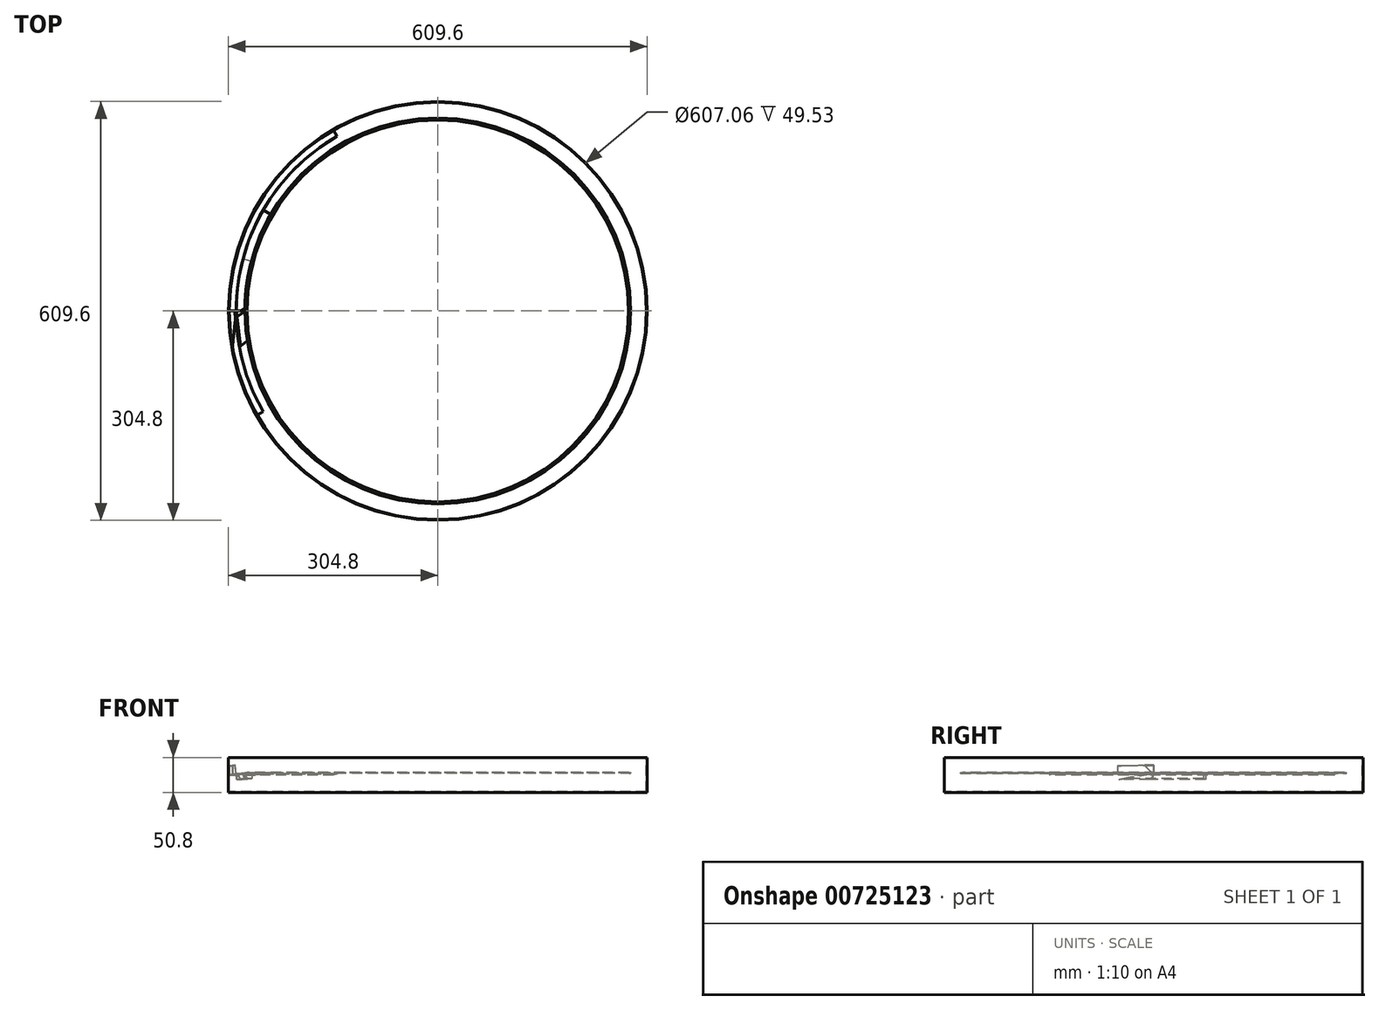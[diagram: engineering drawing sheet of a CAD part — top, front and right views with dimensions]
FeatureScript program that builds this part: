
annotation { "Feature Type Name" : "Feature", "Feature Type Description" : "" }
export const myFeature = defineFeature(function(context is Context, id is Id, definition is map)
    precondition{}
    {
        {
            var Q0;
            Q0=qCreatedBy(makeId("Front.planeOp"),FACE);
            var sketch = newSketch(context, id + "F0", { "sketchPlane" : qUnion([Q0])});
            skLineSegment(sketch, "E0.left", {"start": v(-304.8, -3.12) * mm, "end": v(-304.8, -28.52) * mm});
            skPoint(sketch, "E1.orphan", {"position": v(-304.8, 0) * mm});
            skLineSegment(sketch, "E2", {"start": v(-304.8, -3.12) * mm, "end": v(-304.8, 22.28) * mm});
            skLineSegment(sketch, "E3", {"start": v(-304.8, 22.28) * mm, "end": v(-303.53, 22.28) * mm});
            skLineSegment(sketch, "E4", {"start": v(-303.53, 22.28) * mm, "end": v(-303.53, -2.74) * mm});
            skLineSegment(sketch, "E5", {"start": v(-304.8, -28.52) * mm, "end": v(0, -28.52) * mm});
            skLineSegment(sketch, "E6", {"start": v(-303.53, -27.25) * mm, "end": v(-303.53, -4.1) * mm});
            skLineSegment(sketch, "E7", {"start": v(-303.53, -27.25) * mm, "end": v(0, -27.25) * mm});
            skLineSegment(sketch, "E8", {"start": v(0, -28.52) * mm, "end": v(0, -27.25) * mm});
            skLineSegment(sketch, "E9", {"start": v(-296.67, -1.9) * mm, "end": v(-293.52, -1.5) * mm});
            skLineSegment(sketch, "E10", {"start": v(-303.53, -2.74) * mm, "end": v(-303.53, -4.1) * mm});
            skLineSegment(sketch, "E11", {"start": v(-296.57, -2.75) * mm, "end": v(-293.42, -2.36) * mm});
            skLineSegment(sketch, "E12", {"start": v(-293.52, -1.5) * mm, "end": v(-293.42, -2.36) * mm});
            skLineSegment(sketch, "E13", {"start": v(-280.92, 0.04) * mm, "end": v(-277.76, 0.43) * mm});
            skLineSegment(sketch, "E14", {"start": v(-277.76, 0.43) * mm, "end": v(-277.66, -0.42) * mm});
            skLineSegment(sketch, "E15", {"start": v(-280.92, 0.04) * mm, "end": v(-280.81, -0.81) * mm});
            skLineSegment(sketch, "E16", {"start": v(-280.81, -0.81) * mm, "end": v(-277.66, -0.42) * mm});
            skLineSegment(sketch, "E17", {"start": v(-293.52, -1.5) * mm, "end": v(-280.92, 0.04) * mm});
            skLineSegment(sketch, "E18", {"start": v(-293.42, -2.36) * mm, "end": v(-280.81, -0.81) * mm});
            skLineSegment(sketch, "E19", {"start": v(-296.67, -1.9) * mm, "end": v(-303.53, -2.74) * mm});
            skLineSegment(sketch, "E20", {"start": v(-298.22, 10.7) * mm, "end": v(-303.53, 10.06) * mm});
            skLineSegment(sketch, "E21", {"start": v(-293.52, -1.5) * mm, "end": v(-295.07, 11.1) * mm});
            skLineSegment(sketch, "E22", {"start": v(-298.22, 10.7) * mm, "end": v(-295.07, 11.1) * mm});
            skLineSegment(sketch, "E23", {"start": v(-296.57, -2.75) * mm, "end": v(-303.53, -3.6) * mm});
            skLineSegment(sketch, "E24", {"start": v(-293.42, -2.36) * mm, "end": v(-292.49, -9.92) * mm});
            skLineSegment(sketch, "E25", {"start": v(-292.49, -9.92) * mm, "end": v(-279.88, -8.37) * mm});
            skLineSegment(sketch, "E26", {"start": v(-280.81, -0.81) * mm, "end": v(-279.88, -8.37) * mm});
            skSolve(sketch);
        }
        {
            var Q0;
            Q0=qCreatedBy(makeId("Front.planeOp"),FACE);
            var sketch = newSketch(context, id + "F1", { "sketchPlane" : qUnion([Q0])});
            skLineSegment(sketch, "E27", {"start": v(0, 40.5) * mm, "end": v(0, -62.38) * mm});
            skSolve(sketch);
        }
        {
            var Q0;
            Q0=makeQuery(id+"F0.imprint","IMPRINT",FACE,{"disambiguationData":[TD([[makeQuery(id+"F0.imprint","IMPRINT",EDGE,{"derivedFrom":sQuery(id+"F0.wireOp",EDGE,"E0.left")}),1.0]])]});
            var Q1;
            Q1=sQuery(id+"F1.wireOp",EDGE,"E27");
            revolve(context, id + "F2", {"surfaceOperationType" : NewSurfaceOperationType.NEW, "entities" : qUnion([Q0]), "axis" : qUnion([Q1]), "revolveType" : RevolveType.FULL});
        }
        {
            var Q0;
            Q0=makeQuery(id+"F2.opRevolve","SWEPT_FACE",FACE,{"disambiguationData":[OSD([sQuery(id+"F0.wireOp",EDGE,"E7")])]});
            var sketch = newSketch(context, id + "F3", { "sketchPlane" : qUnion([Q0])});
            skLineSegment(sketch, "E28", {"start": v(-303.53, 0) * mm, "end": v(-273.66, 78.17) * mm});
            skLineSegment(sketch, "E29", {"start": v(-273.66, 78.17) * mm, "end": v(-273.66, -3.17) * mm});
            skLineSegment(sketch, "E30", {"start": v(-273.66, -3.17) * mm, "end": v(-303.53, 0) * mm});
            skSolve(sketch);
        }
        {
            var Q0;
            Q0=makeQuery(id+"F0.imprint","IMPRINT",FACE,{"disambiguationData":[TD([[makeQuery(id+"F0.imprint","IMPRINT",EDGE,{"derivedFrom":sQuery(id+"F0.wireOp",EDGE,"E12")}),1.0]])]});
            var Q1;
            Q1=sQuery(id+"F1.wireOp",EDGE,"E27");
            revolve(context, id + "F4", {"surfaceOperationType" : NewSurfaceOperationType.NEW, "entities" : qUnion([Q0]), "axis" : qUnion([Q1]), "revolveType" : RevolveType.ONE_DIRECTION, "angle" : 30 * degree});
        }
        {
            var Q0;
            Q0=makeQuery(id+"F0.imprint","IMPRINT",FACE,{"disambiguationData":[TD([[makeQuery(id+"F0.imprint","IMPRINT",EDGE,{"derivedFrom":sQuery(id+"F0.wireOp",EDGE,"E18")}),-1.0]])]});
            var Q1;
            Q1=sQuery(id+"F1.wireOp",EDGE,"E27");
            revolve(context, id + "F5", {"operationType" : NewBodyOperationType.ADD, "surfaceOperationType" : NewSurfaceOperationType.NEW, "entities" : qUnion([Q0]), "axis" : qUnion([Q1]), "revolveType" : RevolveType.TWO_DIRECTIONS, "angle" : 15 * degree, "angleBack" : 350 * degree});
        }
        {
            var Q0;
            Q0=qCreatedBy(makeId("Right.planeOp"),FACE);
            var sketch = newSketch(context, id + "F6", { "sketchPlane" : qUnion([Q0])});
            skLineSegment(sketch, "E31", {"start": v(-52.64, -10.07) * mm, "end": v(6.2, 0.4) * mm});
            skLineSegment(sketch, "E32", {"start": v(6.2, 0.4) * mm, "end": v(-53.05, 0.4) * mm});
            skLineSegment(sketch, "E33", {"start": v(-53.05, 0.4) * mm, "end": v(-52.64, -10.07) * mm});
            skSolve(sketch);
        }
        {
            var Q0;
            Q0=makeQuery(id+"F6.imprint","IMPRINT",FACE,{"disambiguationData":[TD([[makeQuery(id+"F6.imprint","IMPRINT",EDGE,{"derivedFrom":sQuery(id+"F6.wireOp",EDGE,"E31")}),1.0]])]});
            extrude(context, id + "F7", {"entities" : qUnion([Q0]), "operationType" : NewBodyOperationType.REMOVE, "oppositeDirection" : true, "depth" : 294.64 * mm, "offsetDistance" : 25.4 * mm});
        }
        {
            var Q0;
            Q0=makeQuery(id+"F0.imprint","IMPRINT",FACE,{"disambiguationData":[TD([[makeQuery(id+"F0.imprint","IMPRINT",EDGE,{"derivedFrom":sQuery(id+"F0.wireOp",EDGE,"E13")}),-1.0]])]});
            var Q1;
            Q1=sQuery(id+"F1.wireOp",EDGE,"E27");
            revolve(context, id + "F8", {"surfaceOperationType" : NewSurfaceOperationType.NEW, "entities" : qUnion([Q0]), "axis" : qUnion([Q1]), "revolveType" : RevolveType.FULL});
        }
        {
            var Q0;
            Q0=makeQuery(id+"F0.imprint","IMPRINT",FACE,{"disambiguationData":[TD([[makeQuery(id+"F0.imprint","IMPRINT",EDGE,{"derivedFrom":sQuery(id+"F0.wireOp",EDGE,"E9")}),1.0]])]});
            var Q1;
            Q1=sQuery(id+"F1.wireOp",EDGE,"E27");
            revolve(context, id + "F9", {"surfaceOperationType" : NewSurfaceOperationType.NEW, "entities" : qUnion([Q0]), "axis" : qUnion([Q1]), "revolveType" : RevolveType.TWO_DIRECTIONS, "angle" : 0 * degree, "angleBack" : 350 * degree});
        }
        {
            var Q0;
            Q0=makeQuery(id+"F3.imprint","IMPRINT",FACE,{"disambiguationData":[TD([[makeQuery(id+"F3.imprint","IMPRINT",EDGE,{"derivedFrom":sQuery(id+"F3.wireOp",EDGE,"E28")}),1.0]])]});
            var sketch = newSketch(context, id + "F10", { "sketchPlane" : qUnion([Q0])});
            skLineSegment(sketch, "E34", {"start": v(-298.78, -52.64) * mm, "end": v(-293.31, 1.39) * mm});
            skLineSegment(sketch, "E35", {"start": v(-293.31, 1.39) * mm, "end": v(-286.77, -52.44) * mm});
            skLineSegment(sketch, "E36", {"start": v(-286.77, -52.44) * mm, "end": v(-298.78, -52.64) * mm});
            skSolve(sketch);
        }
        {
            var Q0;
            {var subQ0=sQuery(id+"F10.wireOp",EDGE,"E36");Q0=makeQuery(id+"F10.imprint","IMPRINT",FACE,{"disambiguationData":[TD([[makeQuery(id+"F10.imprint","IMPRINT",EDGE,{"derivedFrom":subQ0}),-1.0]])]});}
            var Q1;
            Q1=makeQuery(id+"F9.opRevolve","SWEPT_FACE",FACE,{"disambiguationData":[OSD([sQuery(id+"F0.wireOp",EDGE,"E20"),sQuery(id+"F0.wireOp",EDGE,"E22")])]});
            extrude(context, id + "F11", {"entities" : qUnion([Q0]), "operationType" : NewBodyOperationType.REMOVE, "endBound" : BoundingType.UP_TO_SURFACE, "depth" : 50.8 * mm, "endBoundEntityFace" : qUnion([Q1]), "offsetDistance" : 25.4 * mm});
        }
        {
            var Q0;
            Q0=makeQuery(id+"F0.imprint","IMPRINT",FACE,{"disambiguationData":[TD([[makeQuery(id+"F0.imprint","IMPRINT",EDGE,{"derivedFrom":sQuery(id+"F0.wireOp",EDGE,"pQ6oDv7N-JJg5-aNj2-zSGn-AvQwwp5hPYC0")}),1.0]])]});
            var Q1;
            Q1=makeQuery(id+"F0.imprint","IMPRINT",FACE,{"disambiguationData":[TD([[makeQuery(id+"F0.imprint","IMPRINT",EDGE,{"derivedFrom":sQuery(id+"F0.wireOp",EDGE,"E9")}),-1.0]])]});
            var Q2;
            Q2=sQuery(id+"F1.wireOp",EDGE,"E27");
            revolve(context, id + "F12", {"surfaceOperationType" : NewSurfaceOperationType.NEW, "entities" : qUnion([Q0, Q1]), "axis" : qUnion([Q2]), "revolveType" : RevolveType.TWO_DIRECTIONS, "angle" : 60 * degree, "angleBack" : 330 * degree});
        }
    });
